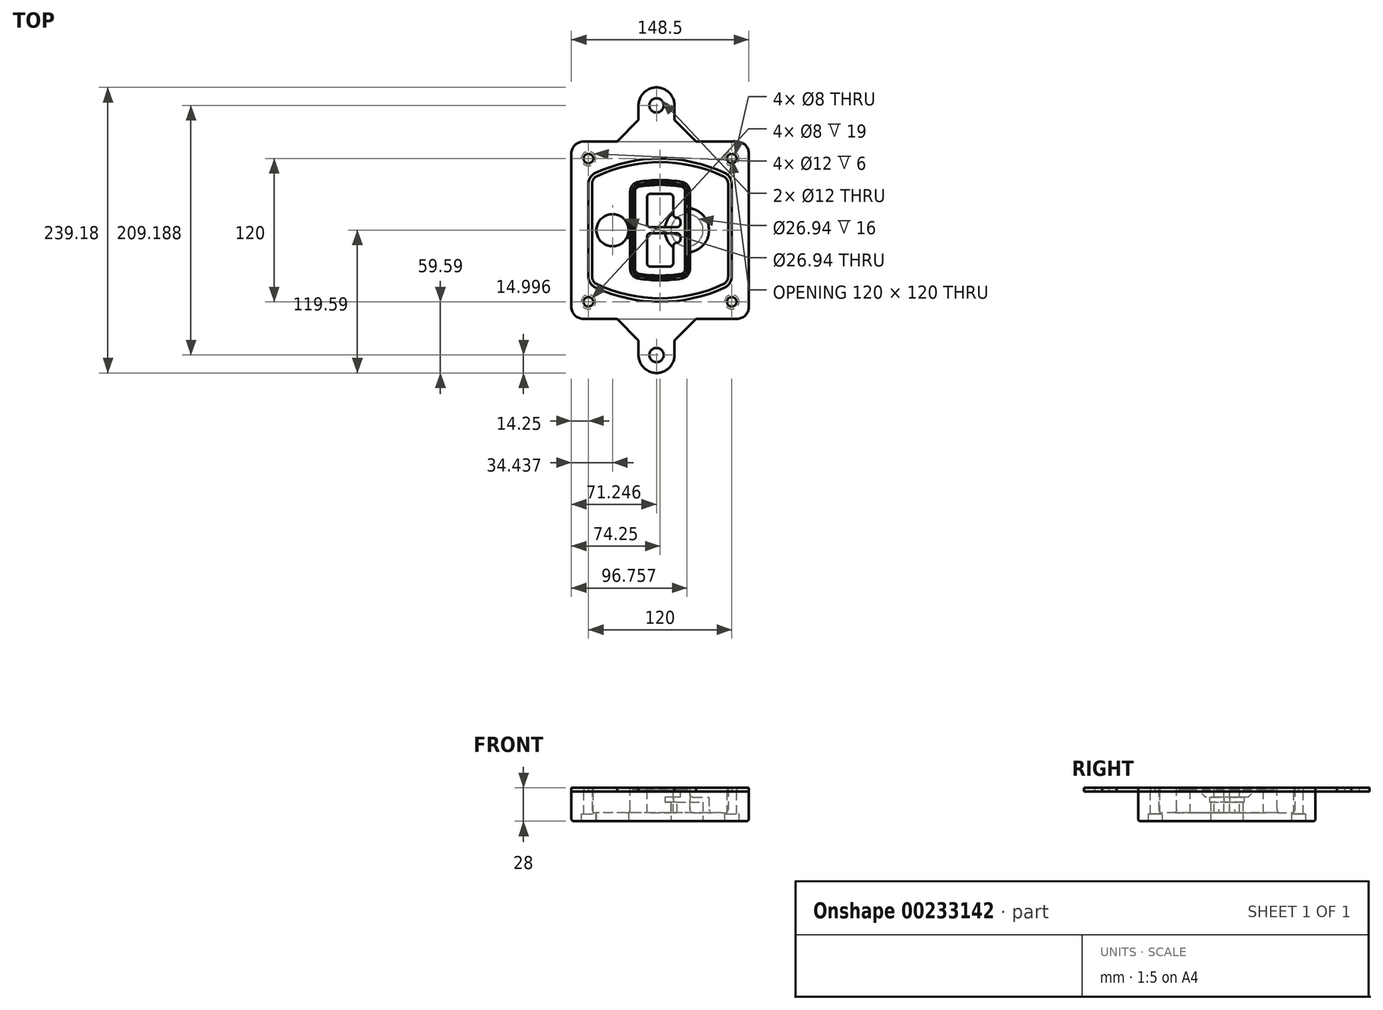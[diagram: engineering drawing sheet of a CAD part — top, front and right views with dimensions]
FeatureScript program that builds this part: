
annotation { "Feature Type Name" : "Feature", "Feature Type Description" : "" }
export const myFeature = defineFeature(function(context is Context, id is Id, definition is map)
    precondition{}
    {
        {
            var Q0;
            Q0=qCreatedBy(makeId("Top.planeOp"),FACE);
            var sketch = newSketch(context, id + "F0", { "sketchPlane" : qUnion([Q0])});
            skPoint(sketch, "E0.rect.middle", {"position": v(0, 0) * mm});
            skLineSegment(sketch, "E1.bottom", {"start": v(-64.25, -74.25) * mm, "end": v(64.25, -74.25) * mm});
            skLineSegment(sketch, "E1.top", {"start": v(-64.25, 74.25) * mm, "end": v(64.25, 74.25) * mm});
            skLineSegment(sketch, "E1.left", {"start": v(-74.25, -64.25) * mm, "end": v(-74.25, 64.25) * mm});
            skLineSegment(sketch, "E1.right", {"start": v(74.25, -64.25) * mm, "end": v(74.25, 64.25) * mm});
            skLineSegment(sketch, "E2", {"start": v(-74.25, 74.25) * mm, "end": v(74.25, -74.25) * mm, "construction": true});
            skLineSegment(sketch, "E3", {"start": v(74.25, 74.25) * mm, "end": v(-74.25, -74.25) * mm, "construction": true});
            skCircle(sketch, "E4", {"center": v(-60, 60) * mm, "radius": 4 * mm});
            skCircle(sketch, "E5", {"center": v(60, 60) * mm, "radius": 4 * mm});
            skCircle(sketch, "E6", {"center": v(60, -60) * mm, "radius": 4 * mm});
            skCircle(sketch, "E7", {"center": v(-60, -60) * mm, "radius": 4 * mm});
            skLineSegment(sketch, "E8", {"start": v(-60, 60) * mm, "end": v(60, 60) * mm, "construction": true});
            skLineSegment(sketch, "E9", {"start": v(60, 60) * mm, "end": v(60, -60) * mm, "construction": true});
            skLineSegment(sketch, "E10", {"start": v(60, -60) * mm, "end": v(-60, -60) * mm, "construction": true});
            skLineSegment(sketch, "E11", {"start": v(-60, -60) * mm, "end": v(-60, 60) * mm, "construction": true});
            skLineSegment(sketch, "E12", {"start": v(-60, 38.83) * mm, "end": v(-60, -38.83) * mm});
            skLineSegment(sketch, "E13", {"start": v(60, 38.83) * mm, "end": v(60, -38.83) * mm});
            skArc(sketch, "E14", {"start": v(54.26, 47.88) * mm, "mid": v(0, 60) * mm, "end": v(-54.26, 47.88) * mm});
            skArc(sketch, "E15", {"start": v(-54.26, -47.88) * mm, "mid": v(0, -60) * mm, "end": v(54.26, -47.88) * mm});
            skLineSegment(sketch, "E16", {"start": v(-60, 0) * mm, "end": v(60, 0) * mm, "construction": true});
            skPoint(sketch, "E17.visualSharp", {"position": v(-60, -45) * mm});
            skArc(sketch, "E17.filletArc", {"start": v(-60, -38.83) * mm, "mid": v(-58.44, -44.2) * mm, "end": v(-54.26, -47.88) * mm});
            skPoint(sketch, "E18.visualSharp", {"position": v(-60, 45) * mm});
            skArc(sketch, "E18.filletArc", {"start": v(-54.26, 47.88) * mm, "mid": v(-58.44, 44.2) * mm, "end": v(-60, 38.83) * mm});
            skPoint(sketch, "E19.visualSharp", {"position": v(60, 45) * mm});
            skArc(sketch, "E19.filletArc", {"start": v(60, 38.83) * mm, "mid": v(58.44, 44.2) * mm, "end": v(54.26, 47.88) * mm});
            skPoint(sketch, "E20.visualSharp", {"position": v(60, -45) * mm});
            skArc(sketch, "E20.filletArc", {"start": v(54.26, -47.88) * mm, "mid": v(58.44, -44.2) * mm, "end": v(60, -38.83) * mm});
            skPoint(sketch, "E21.visualSharp", {"position": v(-74.25, 74.25) * mm});
            skArc(sketch, "E21.filletArc", {"start": v(-64.25, 74.25) * mm, "mid": v(-71.32, 71.32) * mm, "end": v(-74.25, 64.25) * mm});
            skPoint(sketch, "E22.visualSharp", {"position": v(74.25, 74.25) * mm});
            skArc(sketch, "E22.filletArc", {"start": v(74.25, 64.25) * mm, "mid": v(71.32, 71.32) * mm, "end": v(64.25, 74.25) * mm});
            skPoint(sketch, "E23.visualSharp", {"position": v(74.25, -74.25) * mm});
            skArc(sketch, "E23.filletArc", {"start": v(64.25, -74.25) * mm, "mid": v(71.32, -71.32) * mm, "end": v(74.25, -64.25) * mm});
            skPoint(sketch, "E24.visualSharp", {"position": v(-74.25, -74.25) * mm});
            skArc(sketch, "E24.filletArc", {"start": v(-74.25, -64.25) * mm, "mid": v(-71.32, -71.32) * mm, "end": v(-64.25, -74.25) * mm});
            skArc(sketch, "E25.0", {"start": v(57, 38.83) * mm, "mid": v(55.9, 42.58) * mm, "end": v(52.98, 45.17) * mm});
            skLineSegment(sketch, "E25.1", {"start": v(57, 38.83) * mm, "end": v(57, -38.83) * mm});
            skArc(sketch, "E25.2", {"start": v(52.98, -45.17) * mm, "mid": v(55.9, -42.58) * mm, "end": v(57, -38.83) * mm});
            skArc(sketch, "E25.3", {"start": v(-52.98, -45.17) * mm, "mid": v(0, -57) * mm, "end": v(52.98, -45.17) * mm});
            skArc(sketch, "E25.4", {"start": v(-57, -38.83) * mm, "mid": v(-55.9, -42.58) * mm, "end": v(-52.98, -45.17) * mm});
            skArc(sketch, "E25.5", {"start": v(52.98, 45.17) * mm, "mid": v(0, 57) * mm, "end": v(-52.98, 45.17) * mm});
            skLineSegment(sketch, "E25.6", {"start": v(-57, 38.83) * mm, "end": v(-57, -38.83) * mm});
            skArc(sketch, "E25.7", {"start": v(-52.98, 45.17) * mm, "mid": v(-55.9, 42.58) * mm, "end": v(-57, 38.83) * mm});
            skArc(sketch, "E26.0", {"start": v(-55.96, 51.5) * mm, "mid": v(-61.82, 46.33) * mm, "end": v(-64, 38.83) * mm});
            skArc(sketch, "E26.1", {"start": v(55.96, 51.5) * mm, "mid": v(0, 64) * mm, "end": v(-55.96, 51.5) * mm});
            skArc(sketch, "E26.2", {"start": v(64, 38.83) * mm, "mid": v(61.82, 46.33) * mm, "end": v(55.96, 51.5) * mm});
            skLineSegment(sketch, "E26.3", {"start": v(64, 38.83) * mm, "end": v(64, -38.83) * mm});
            skArc(sketch, "E26.4", {"start": v(55.96, -51.5) * mm, "mid": v(61.82, -46.33) * mm, "end": v(64, -38.83) * mm});
            skLineSegment(sketch, "E26.5", {"start": v(-64, 38.83) * mm, "end": v(-64, -38.83) * mm});
            skArc(sketch, "E26.6", {"start": v(-55.96, -51.5) * mm, "mid": v(0, -64) * mm, "end": v(55.96, -51.5) * mm});
            skArc(sketch, "E26.7", {"start": v(-64, -38.83) * mm, "mid": v(-61.82, -46.33) * mm, "end": v(-55.96, -51.5) * mm});
            skSolve(sketch);
        }
        {
            var Q0;
            Q0=makeQuery(id+"F0.imprint","IMPRINT",FACE,{"disambiguationData":[TD([[makeQuery(id+"F0.imprint","IMPRINT",EDGE,{"derivedFrom":sQuery(id+"F0.wireOp",EDGE,"E1.bottom")}),1.0]])]});
            var Q1;
            Q1=makeQuery(id+"F0.imprint","IMPRINT",FACE,{"disambiguationData":[TD([[makeQuery(id+"F0.imprint","IMPRINT",EDGE,{"derivedFrom":sQuery(id+"F0.wireOp",EDGE,"E12")}),1.0]])]});
            var Q2;
            Q2=makeQuery(id+"F0.imprint","IMPRINT",FACE,{"disambiguationData":[TD([[makeQuery(id+"F0.imprint","IMPRINT",EDGE,{"derivedFrom":sQuery(id+"F0.wireOp",EDGE,"E25.0")}),1.0]])]});
            var Q3;
            Q3=makeQuery(id+"F0.imprint","IMPRINT",FACE,{"disambiguationData":[TD([[makeQuery(id+"F0.imprint","IMPRINT",EDGE,{"derivedFrom":sQuery(id+"F0.wireOp",EDGE,"E12")}),-1.0]])]});
            extrude(context, id + "F1", {"entities" : qUnion([Q0, Q1, Q2, Q3]), "oppositeDirection" : true, "depth" : 25 * mm});
        }
        {
            var Q0;
            Q0=makeQuery(id+"F0.imprint","IMPRINT",FACE,{"disambiguationData":[TD([[makeQuery(id+"F0.imprint","IMPRINT",EDGE,{"derivedFrom":sQuery(id+"F0.wireOp",EDGE,"E12")}),1.0]])]});
            extrude(context, id + "F2", {"entities" : qUnion([Q0]), "operationType" : NewBodyOperationType.ADD, "depth" : 3 * mm});
        }
        {
            var Q0;
            Q0=makeQuery(id+"F0.imprint","IMPRINT",FACE,{"disambiguationData":[TD([[makeQuery(id+"F0.imprint","IMPRINT",EDGE,{"derivedFrom":sQuery(id+"F0.wireOp",EDGE,"E25.0")}),1.0]])]});
            extrude(context, id + "F3", {"entities" : qUnion([Q0]), "operationType" : NewBodyOperationType.REMOVE, "oppositeDirection" : true, "depth" : 18 * mm});
        }
        {
            var Q0;
            Q0=makeQuery(id+"F2.opExtrude","CAP_FACE",FACE,{"disambiguationData":[OSD([sQuery(id+"F0.wireOp",EDGE,"E12"),sQuery(id+"F0.wireOp",EDGE,"E13"),sQuery(id+"F0.wireOp",EDGE,"E14"),sQuery(id+"F0.wireOp",EDGE,"E15"),sQuery(id+"F0.wireOp",EDGE,"E17.filletArc"),sQuery(id+"F0.wireOp",EDGE,"E18.filletArc"),sQuery(id+"F0.wireOp",EDGE,"E19.filletArc"),sQuery(id+"F0.wireOp",EDGE,"E20.filletArc"),sQuery(id+"F0.wireOp",EDGE,"E25.0"),sQuery(id+"F0.wireOp",EDGE,"E25.1"),sQuery(id+"F0.wireOp",EDGE,"E25.2"),sQuery(id+"F0.wireOp",EDGE,"E25.3"),sQuery(id+"F0.wireOp",EDGE,"E25.4"),sQuery(id+"F0.wireOp",EDGE,"E25.5"),sQuery(id+"F0.wireOp",EDGE,"E25.6"),sQuery(id+"F0.wireOp",EDGE,"E25.7")])],"isStart":false});
            var sketch = newSketch(context, id + "F4", { "sketchPlane" : qUnion([Q0])});
            skArc(sketch, "E27.0", {"start": v(-18.34, -40.45) * mm, "mid": v(0, -42) * mm, "end": v(18.34, -40.45) * mm});
            skArc(sketch, "E28.0", {"start": v(18.34, 40.45) * mm, "mid": v(0, 42) * mm, "end": v(-18.34, 40.45) * mm});
            skLineSegment(sketch, "E29", {"start": v(-25, 32.57) * mm, "end": v(-25, -32.57) * mm});
            skLineSegment(sketch, "E30", {"start": v(25, 32.57) * mm, "end": v(25, -32.57) * mm});
            skLineSegment(sketch, "E31", {"start": v(-25, 39.1) * mm, "end": v(25, 39.1) * mm, "construction": true});
            skLineSegment(sketch, "E32", {"start": v(-25, -39.1) * mm, "end": v(25, -39.1) * mm, "construction": true});
            skPoint(sketch, "E33.visualSharp", {"position": v(-25, 39.1) * mm});
            skArc(sketch, "E33.filletArc", {"start": v(-18.34, 40.45) * mm, "mid": v(-23.11, 37.73) * mm, "end": v(-25, 32.57) * mm});
            skPoint(sketch, "E34.visualSharp", {"position": v(25, 39.1) * mm});
            skArc(sketch, "E34.filletArc", {"start": v(25, 32.57) * mm, "mid": v(23.11, 37.73) * mm, "end": v(18.34, 40.45) * mm});
            skPoint(sketch, "E35.visualSharp", {"position": v(25, -39.1) * mm});
            skArc(sketch, "E35.filletArc", {"start": v(18.34, -40.45) * mm, "mid": v(23.11, -37.73) * mm, "end": v(25, -32.57) * mm});
            skPoint(sketch, "E36.visualSharp", {"position": v(-25, -39.1) * mm});
            skArc(sketch, "E36.filletArc", {"start": v(-25, -32.57) * mm, "mid": v(-23.11, -37.73) * mm, "end": v(-18.34, -40.45) * mm});
            skArc(sketch, "E37.0", {"start": v(52.98, 45.17) * mm, "mid": v(0, 57) * mm, "end": v(-52.98, 45.17) * mm});
            skArc(sketch, "E37.1", {"start": v(-52.98, 45.17) * mm, "mid": v(-55.9, 42.58) * mm, "end": v(-57, 38.83) * mm});
            skLineSegment(sketch, "E37.2", {"start": v(-57, 38.83) * mm, "end": v(-57, -38.83) * mm});
            skArc(sketch, "E37.3", {"start": v(-57, -38.83) * mm, "mid": v(-55.9, -42.58) * mm, "end": v(-52.98, -45.17) * mm});
            skArc(sketch, "E37.4", {"start": v(-52.98, -45.17) * mm, "mid": v(0, -57) * mm, "end": v(52.98, -45.17) * mm});
            skArc(sketch, "E37.5", {"start": v(52.98, -45.17) * mm, "mid": v(55.9, -42.58) * mm, "end": v(57, -38.83) * mm});
            skLineSegment(sketch, "E37.6", {"start": v(57, 38.83) * mm, "end": v(57, -38.83) * mm});
            skArc(sketch, "E37.7", {"start": v(57, 38.83) * mm, "mid": v(55.9, 42.58) * mm, "end": v(52.98, 45.17) * mm});
            skLineSegment(sketch, "E38.0", {"start": v(23, 32.57) * mm, "end": v(23, -32.57) * mm});
            skArc(sketch, "E38.1", {"start": v(18, -38.48) * mm, "mid": v(21.58, -36.44) * mm, "end": v(23, -32.57) * mm});
            skArc(sketch, "E38.2", {"start": v(-18, -38.48) * mm, "mid": v(0, -40) * mm, "end": v(18, -38.48) * mm});
            skArc(sketch, "E38.3", {"start": v(-23, -32.57) * mm, "mid": v(-21.58, -36.44) * mm, "end": v(-18, -38.48) * mm});
            skLineSegment(sketch, "E38.4", {"start": v(-23, 32.57) * mm, "end": v(-23, -32.57) * mm});
            skArc(sketch, "E38.5", {"start": v(23, 32.57) * mm, "mid": v(21.58, 36.44) * mm, "end": v(18, 38.48) * mm});
            skArc(sketch, "E38.6", {"start": v(-18, 38.48) * mm, "mid": v(-21.58, 36.44) * mm, "end": v(-23, 32.57) * mm});
            skArc(sketch, "E38.7", {"start": v(18, 38.48) * mm, "mid": v(0, 40) * mm, "end": v(-18, 38.48) * mm});
            skArc(sketch, "E39.0", {"start": v(21, 32.57) * mm, "mid": v(20.06, 35.15) * mm, "end": v(17.67, 36.5) * mm});
            skLineSegment(sketch, "E39.1", {"start": v(21, 32.57) * mm, "end": v(21, -32.57) * mm});
            skArc(sketch, "E39.2", {"start": v(17.67, -36.5) * mm, "mid": v(20.06, -35.15) * mm, "end": v(21, -32.57) * mm});
            skArc(sketch, "E39.3", {"start": v(-17.67, -36.5) * mm, "mid": v(0, -38) * mm, "end": v(17.67, -36.5) * mm});
            skArc(sketch, "E39.4", {"start": v(-21, -32.57) * mm, "mid": v(-20.06, -35.15) * mm, "end": v(-17.67, -36.5) * mm});
            skArc(sketch, "E39.5", {"start": v(17.67, 36.5) * mm, "mid": v(0, 38) * mm, "end": v(-17.67, 36.5) * mm});
            skLineSegment(sketch, "E39.6", {"start": v(-21, 32.57) * mm, "end": v(-21, -32.57) * mm});
            skArc(sketch, "E39.7", {"start": v(-17.67, 36.5) * mm, "mid": v(-20.06, 35.15) * mm, "end": v(-21, 32.57) * mm});
            skLineSegment(sketch, "E40", {"start": v(-25, 0) * mm, "end": v(25, 0) * mm, "construction": true});
            skLineSegment(sketch, "E41", {"start": v(-11, 5.5) * mm, "end": v(-11, 27.5) * mm});
            skLineSegment(sketch, "E42", {"start": v(-8, 30.5) * mm, "end": v(8, 30.5) * mm});
            skLineSegment(sketch, "E43", {"start": v(11, 27.5) * mm, "end": v(11, 13.5) * mm});
            skLineSegment(sketch, "E44", {"start": v(14, 10.5) * mm, "end": v(14, 10.5) * mm});
            skLineSegment(sketch, "E45", {"start": v(17, 7.5) * mm, "end": v(17, 5.5) * mm});
            skLineSegment(sketch, "E46", {"start": v(14, 2.5) * mm, "end": v(-8, 2.5) * mm});
            skPoint(sketch, "E47.visualSharp", {"position": v(-11, 30.5) * mm});
            skArc(sketch, "E47.filletArc", {"start": v(-8, 30.5) * mm, "mid": v(-10.12, 29.62) * mm, "end": v(-11, 27.5) * mm});
            skPoint(sketch, "E48.visualSharp", {"position": v(11, 30.5) * mm});
            skArc(sketch, "E48.filletArc", {"start": v(11, 27.5) * mm, "mid": v(10.12, 29.62) * mm, "end": v(8, 30.5) * mm});
            skPoint(sketch, "E49.visualSharp", {"position": v(11, 10.5) * mm});
            skArc(sketch, "E49.filletArc", {"start": v(11, 13.5) * mm, "mid": v(11.88, 11.38) * mm, "end": v(14, 10.5) * mm});
            skPoint(sketch, "E50.visualSharp", {"position": v(17, 10.5) * mm});
            skArc(sketch, "E50.filletArc", {"start": v(17, 7.5) * mm, "mid": v(16.12, 9.62) * mm, "end": v(14, 10.5) * mm});
            skPoint(sketch, "E51.visualSharp", {"position": v(17, 2.5) * mm});
            skArc(sketch, "E51.filletArc", {"start": v(14, 2.5) * mm, "mid": v(16.12, 3.38) * mm, "end": v(17, 5.5) * mm});
            skPoint(sketch, "E52.visualSharp", {"position": v(-11, 2.5) * mm});
            skArc(sketch, "E52.filletArc", {"start": v(-11, 5.5) * mm, "mid": v(-10.12, 3.38) * mm, "end": v(-8, 2.5) * mm});
            skLineSegment(sketch, "E53.0.MirrorCS", {"start": v(14, -2.5) * mm, "end": v(-8, -2.5) * mm});
            skArc(sketch, "E54.0.MirrorCS", {"start": v(-11, -5.5) * mm, "mid": v(-10.12, -3.38) * mm, "end": v(-8, -2.5) * mm});
            skLineSegment(sketch, "E55.0.MirrorCS", {"start": v(-11, -5.5) * mm, "end": v(-11, -27.5) * mm});
            skArc(sketch, "E56.0.MirrorCS", {"start": v(-8, -30.5) * mm, "mid": v(-10.12, -29.62) * mm, "end": v(-11, -27.5) * mm});
            skLineSegment(sketch, "E57.0.MirrorCS", {"start": v(-8, -30.5) * mm, "end": v(8, -30.5) * mm});
            skArc(sketch, "E58.0.MirrorCS", {"start": v(11, -27.5) * mm, "mid": v(10.12, -29.62) * mm, "end": v(8, -30.5) * mm});
            skLineSegment(sketch, "E59.0.MirrorCS", {"start": v(11, -27.5) * mm, "end": v(11, -13.5) * mm});
            skArc(sketch, "E60.0.MirrorCS", {"start": v(11, -13.5) * mm, "mid": v(11.88, -11.38) * mm, "end": v(14, -10.5) * mm});
            skArc(sketch, "E61.0.MirrorCS", {"start": v(17, -7.5) * mm, "mid": v(16.12, -9.62) * mm, "end": v(14, -10.5) * mm});
            skLineSegment(sketch, "E62.0.MirrorCS", {"start": v(17, -7.5) * mm, "end": v(17, -5.5) * mm});
            skArc(sketch, "E63.0.MirrorCS", {"start": v(14, -2.5) * mm, "mid": v(16.12, -3.38) * mm, "end": v(17, -5.5) * mm});
            skSolve(sketch);
        }
        {
            var Q0;
            Q0=makeQuery(id+"F4.imprint","IMPRINT",FACE,{"disambiguationData":[TD([[makeQuery(id+"F4.imprint","IMPRINT",EDGE,{"derivedFrom":sQuery(id+"F4.wireOp",EDGE,"E27.0")}),1.0]])]});
            var Q1;
            Q1=makeQuery(id+"F4.imprint","IMPRINT",FACE,{"disambiguationData":[TD([[makeQuery(id+"F4.imprint","IMPRINT",EDGE,{"derivedFrom":sQuery(id+"F4.wireOp",EDGE,"E38.0")}),-1.0]])]});
            var Q2;
            Q2=makeQuery(id+"F4.imprint","IMPRINT",FACE,{"disambiguationData":[TD([[makeQuery(id+"F4.imprint","IMPRINT",EDGE,{"derivedFrom":sQuery(id+"F4.wireOp",EDGE,"E39.0")}),1.0]])]});
            extrude(context, id + "F5", {"entities" : qUnion([Q0, Q1, Q2]), "operationType" : NewBodyOperationType.ADD, "endBound" : BoundingType.UP_TO_NEXT, "oppositeDirection" : true, "depth" : 25 * mm});
        }
        {
            var Q0;
            Q0=makeQuery(id+"F4.imprint","IMPRINT",FACE,{"disambiguationData":[TD([[makeQuery(id+"F4.imprint","IMPRINT",EDGE,{"derivedFrom":sQuery(id+"F4.wireOp",EDGE,"E38.0")}),-1.0]])]});
            extrude(context, id + "F6", {"entities" : qUnion([Q0]), "operationType" : NewBodyOperationType.REMOVE, "oppositeDirection" : true, "depth" : 2 * mm});
        }
        {
            var Q0;
            Q0=makeQuery(id+"F1.opExtrude","CAP_FACE",FACE,{"disambiguationData":[OSD([sQuery(id+"F0.wireOp",EDGE,"E1.bottom"),sQuery(id+"F0.wireOp",EDGE,"E1.top"),sQuery(id+"F0.wireOp",EDGE,"E1.left"),sQuery(id+"F0.wireOp",EDGE,"E1.right"),sQuery(id+"F0.wireOp",EDGE,"E4"),sQuery(id+"F0.wireOp",EDGE,"E5"),sQuery(id+"F0.wireOp",EDGE,"E6"),sQuery(id+"F0.wireOp",EDGE,"E7"),sQuery(id+"F0.wireOp",EDGE,"E21.filletArc"),sQuery(id+"F0.wireOp",EDGE,"E22.filletArc"),sQuery(id+"F0.wireOp",EDGE,"E23.filletArc"),sQuery(id+"F0.wireOp",EDGE,"E24.filletArc")])],"isStart":false});
            var sketch = newSketch(context, id + "F7", { "sketchPlane" : qUnion([Q0])});
            skCircle(sketch, "E64", {"center": v(22.5, 0) * mm, "radius": 13.47 * mm});
            skCircle(sketch, "E65", {"center": v(-39.81, 0) * mm, "radius": 13.47 * mm});
            skLineSegment(sketch, "E66", {"start": v(74.25, 0) * mm, "end": v(-74.25, 0) * mm});
            skCircle(sketch, "E67", {"center": v(22.5, 0) * mm, "radius": 18.47 * mm});
            skCircle(sketch, "E68", {"center": v(60, -60) * mm, "radius": 6 * mm});
            skCircle(sketch, "E69", {"center": v(-60, -60) * mm, "radius": 6 * mm});
            skCircle(sketch, "E70", {"center": v(-60, 60) * mm, "radius": 6 * mm});
            skCircle(sketch, "E71", {"center": v(60, 60) * mm, "radius": 6 * mm});
            skSolve(sketch);
        }
        {
            var Q0;
            {var subQ1=sQuery(id+"F7.wireOp",EDGE,"E66");var subQ4=sQuery(id+"F7.wireOp",EDGE,"E64");var subQ6=makeQuery(id+"F7.imprint","INTERSECT",VERTEX,{"disambiguationData":[OD(0.0)],"derivedFrom":[subQ4,subQ1]});Q0=makeQuery(id+"F7.imprint","IMPRINT",FACE,{"disambiguationData":[TD([[makeQuery(id+"F7.imprint","IMPRINT",EDGE,{"disambiguationData":[TD([[subQ6,-1.0]])],"derivedFrom":subQ4}),-1.0]])]});}
            var Q1;
            {var subQ0=sQuery(id+"F7.wireOp",EDGE,"E66");var subQ1=sQuery(id+"F7.wireOp",EDGE,"E64");var subQ3=makeQuery(id+"F7.imprint","INTERSECT",VERTEX,{"disambiguationData":[OD(0.0)],"derivedFrom":[subQ1,subQ0]});Q1=makeQuery(id+"F7.imprint","IMPRINT",FACE,{"disambiguationData":[TD([[makeQuery(id+"F7.imprint","IMPRINT",EDGE,{"disambiguationData":[TD([[subQ3,-1.0]])],"derivedFrom":subQ1}),1.0]])]});}
            var Q2;
            {var subQ0=sQuery(id+"F7.wireOp",EDGE,"E66");var subQ1=sQuery(id+"F7.wireOp",EDGE,"E64");var subQ3=makeQuery(id+"F7.imprint","INTERSECT",VERTEX,{"disambiguationData":[OD(0.0)],"derivedFrom":[subQ1,subQ0]});Q2=makeQuery(id+"F7.imprint","IMPRINT",FACE,{"disambiguationData":[TD([[makeQuery(id+"F7.imprint","IMPRINT",EDGE,{"disambiguationData":[TD([[subQ3,1.0]])],"derivedFrom":subQ1}),1.0]])]});}
            var Q3;
            {var subQ1=sQuery(id+"F7.wireOp",EDGE,"E66");var subQ4=sQuery(id+"F7.wireOp",EDGE,"E64");var subQ6=makeQuery(id+"F7.imprint","INTERSECT",VERTEX,{"disambiguationData":[OD(0.0)],"derivedFrom":[subQ4,subQ1]});Q3=makeQuery(id+"F7.imprint","IMPRINT",FACE,{"disambiguationData":[TD([[makeQuery(id+"F7.imprint","IMPRINT",EDGE,{"disambiguationData":[TD([[subQ6,1.0]])],"derivedFrom":subQ4}),-1.0]])]});}
            extrude(context, id + "F8", {"entities" : qUnion([Q0, Q1, Q2, Q3]), "operationType" : NewBodyOperationType.ADD, "oppositeDirection" : true, "depth" : 20 * mm});
        }
        {
            var Q0;
            {var subQ0=sQuery(id+"F7.wireOp",EDGE,"E66");var subQ1=sQuery(id+"F7.wireOp",EDGE,"E64");var subQ3=makeQuery(id+"F7.imprint","INTERSECT",VERTEX,{"disambiguationData":[OD(0.0)],"derivedFrom":[subQ1,subQ0]});Q0=makeQuery(id+"F7.imprint","IMPRINT",FACE,{"disambiguationData":[TD([[makeQuery(id+"F7.imprint","IMPRINT",EDGE,{"disambiguationData":[TD([[subQ3,-1.0]])],"derivedFrom":subQ1}),1.0]])]});}
            var Q1;
            {var subQ0=sQuery(id+"F7.wireOp",EDGE,"E66");var subQ1=sQuery(id+"F7.wireOp",EDGE,"E64");var subQ3=makeQuery(id+"F7.imprint","INTERSECT",VERTEX,{"disambiguationData":[OD(0.0)],"derivedFrom":[subQ1,subQ0]});Q1=makeQuery(id+"F7.imprint","IMPRINT",FACE,{"disambiguationData":[TD([[makeQuery(id+"F7.imprint","IMPRINT",EDGE,{"disambiguationData":[TD([[subQ3,1.0]])],"derivedFrom":subQ1}),1.0]])]});}
            extrude(context, id + "F9", {"entities" : qUnion([Q0, Q1]), "operationType" : NewBodyOperationType.REMOVE, "oppositeDirection" : true, "depth" : 16 * mm});
        }
        {
            var Q0;
            {var subQ0=sQuery(id+"F7.wireOp",EDGE,"E66");var subQ1=sQuery(id+"F7.wireOp",EDGE,"E65");var subQ3=makeQuery(id+"F7.imprint","INTERSECT",VERTEX,{"disambiguationData":[OD(0.0)],"derivedFrom":[subQ1,subQ0]});Q0=makeQuery(id+"F7.imprint","IMPRINT",FACE,{"disambiguationData":[TD([[makeQuery(id+"F7.imprint","IMPRINT",EDGE,{"disambiguationData":[TD([[subQ3,-1.0]])],"derivedFrom":subQ1}),1.0]])]});}
            var Q1;
            {var subQ0=sQuery(id+"F7.wireOp",EDGE,"E66");var subQ1=sQuery(id+"F7.wireOp",EDGE,"E65");var subQ3=makeQuery(id+"F7.imprint","INTERSECT",VERTEX,{"disambiguationData":[OD(0.0)],"derivedFrom":[subQ1,subQ0]});Q1=makeQuery(id+"F7.imprint","IMPRINT",FACE,{"disambiguationData":[TD([[makeQuery(id+"F7.imprint","IMPRINT",EDGE,{"disambiguationData":[TD([[subQ3,1.0]])],"derivedFrom":subQ1}),1.0]])]});}
            extrude(context, id + "F10", {"entities" : qUnion([Q0, Q1]), "operationType" : NewBodyOperationType.REMOVE, "oppositeDirection" : true, "depth" : 25 * mm});
        }
        {
            var Q0;
            Q0=makeQuery(id+"F7.imprint","IMPRINT",FACE,{"disambiguationData":[TD([[makeQuery(id+"F7.imprint","IMPRINT",EDGE,{"derivedFrom":sQuery(id+"F7.wireOp",EDGE,"E68")}),1.0]])]});
            var Q1;
            Q1=makeQuery(id+"F7.imprint","IMPRINT",FACE,{"disambiguationData":[TD([[makeQuery(id+"F7.imprint","IMPRINT",EDGE,{"derivedFrom":makeQuery(id+"F1.opExtrude","CAP_EDGE",EDGE,{"disambiguationData":[OSD([sQuery(id+"F0.wireOp",EDGE,"E5")])],"isStart":false})}),-1.0]])]});
            var Q2;
            Q2=makeQuery(id+"F7.imprint","IMPRINT",FACE,{"disambiguationData":[TD([[makeQuery(id+"F7.imprint","IMPRINT",EDGE,{"derivedFrom":sQuery(id+"F7.wireOp",EDGE,"E69")}),1.0]])]});
            var Q3;
            Q3=makeQuery(id+"F7.imprint","IMPRINT",FACE,{"disambiguationData":[TD([[makeQuery(id+"F7.imprint","IMPRINT",EDGE,{"derivedFrom":makeQuery(id+"F1.opExtrude","CAP_EDGE",EDGE,{"disambiguationData":[OSD([sQuery(id+"F0.wireOp",EDGE,"E4")])],"isStart":false})}),-1.0]])]});
            var Q4;
            Q4=makeQuery(id+"F7.imprint","IMPRINT",FACE,{"disambiguationData":[TD([[makeQuery(id+"F7.imprint","IMPRINT",EDGE,{"derivedFrom":sQuery(id+"F7.wireOp",EDGE,"E70")}),1.0]])]});
            var Q5;
            Q5=makeQuery(id+"F7.imprint","IMPRINT",FACE,{"disambiguationData":[TD([[makeQuery(id+"F7.imprint","IMPRINT",EDGE,{"derivedFrom":makeQuery(id+"F1.opExtrude","CAP_EDGE",EDGE,{"disambiguationData":[OSD([sQuery(id+"F0.wireOp",EDGE,"E7")])],"isStart":false})}),-1.0]])]});
            var Q6;
            Q6=makeQuery(id+"F7.imprint","IMPRINT",FACE,{"disambiguationData":[TD([[makeQuery(id+"F7.imprint","IMPRINT",EDGE,{"derivedFrom":sQuery(id+"F7.wireOp",EDGE,"E71")}),1.0]])]});
            var Q7;
            Q7=makeQuery(id+"F7.imprint","IMPRINT",FACE,{"disambiguationData":[TD([[makeQuery(id+"F7.imprint","IMPRINT",EDGE,{"derivedFrom":makeQuery(id+"F1.opExtrude","CAP_EDGE",EDGE,{"disambiguationData":[OSD([sQuery(id+"F0.wireOp",EDGE,"E6")])],"isStart":false})}),-1.0]])]});
            extrude(context, id + "F11", {"entities" : qUnion([Q0, Q1, Q2, Q3, Q4, Q5, Q6, Q7]), "operationType" : NewBodyOperationType.REMOVE, "oppositeDirection" : true, "depth" : 6 * mm});
        }
        {
            var Q0;
            Q0=makeQuery(id+"F9.boolean.opBoolean","COPY",FACE,{"derivedFrom":makeQuery(id+"F9.opExtrude","CAP_FACE",FACE,{"disambiguationData":[OSD([sQuery(id+"F7.wireOp",EDGE,"E64")])],"isStart":false})});
            var sketch = newSketch(context, id + "F12", { "sketchPlane" : qUnion([Q0])});
            skArc(sketch, "E72.0", {"start": v(11, 14.45) * mm, "mid": v(6.45, 9.13) * mm, "end": v(4.2, 2.5) * mm});
            skArc(sketch, "E72.1", {"start": v(4.2, -2.5) * mm, "mid": v(6.45, -9.13) * mm, "end": v(11, -14.45) * mm});
            skLineSegment(sketch, "E73", {"start": v(4.2, -2.5) * mm, "end": v(14, -2.5) * mm});
            skLineSegment(sketch, "E74.0", {"start": v(14, 2.5) * mm, "end": v(4.2, 2.5) * mm});
            skArc(sketch, "E74.1", {"start": v(14, 2.5) * mm, "mid": v(16.12, 3.38) * mm, "end": v(17, 5.5) * mm});
            skLineSegment(sketch, "E74.2", {"start": v(17, 7.5) * mm, "end": v(17, 5.5) * mm});
            skArc(sketch, "E74.3", {"start": v(17, 7.5) * mm, "mid": v(16.12, 9.62) * mm, "end": v(14, 10.5) * mm});
            skArc(sketch, "E74.4", {"start": v(11, 13.5) * mm, "mid": v(11.88, 11.38) * mm, "end": v(14, 10.5) * mm});
            skLineSegment(sketch, "E74.5", {"start": v(11, 14.45) * mm, "end": v(11, 13.5) * mm});
            skLineSegment(sketch, "E74.7", {"start": v(14, -2.5) * mm, "end": v(4.2, -2.5) * mm});
            skArc(sketch, "E74.8", {"start": v(14, -2.5) * mm, "mid": v(16.12, -3.38) * mm, "end": v(17, -5.5) * mm});
            skLineSegment(sketch, "E74.9", {"start": v(17, -7.5) * mm, "end": v(17, -5.5) * mm});
            skArc(sketch, "E74.10", {"start": v(17, -7.5) * mm, "mid": v(16.12, -9.62) * mm, "end": v(14, -10.5) * mm});
            skArc(sketch, "E74.11", {"start": v(11, -13.5) * mm, "mid": v(11.88, -11.38) * mm, "end": v(14, -10.5) * mm});
            skLineSegment(sketch, "E74.12", {"start": v(11, -14.45) * mm, "end": v(11, -13.5) * mm});
            skPoint(sketch, "E75.orphan", {"position": v(11, -27.5) * mm});
            skPoint(sketch, "E76.orphan", {"position": v(-8, -2.5) * mm});
            skPoint(sketch, "E77.orphan", {"position": v(-8, 2.5) * mm});
            skPoint(sketch, "E78.orphan", {"position": v(11, 27.5) * mm});
            skSolve(sketch);
        }
        {
            var Q0;
            {var subQ7=sQuery(id+"F12.wireOp",EDGE,"E72.0");var subQ14=sQuery(id+"F12.wireOp",EDGE,"E72.1");var subQ16=sQuery(id+"F12.wireOp",EDGE,"E74.1");var subQ18=sQuery(id+"F12.wireOp",EDGE,"E74.8");Q0=qUnion([makeQuery(id+"F12.imprint","IMPRINT",FACE,{"disambiguationData":[TD([[makeQuery(id+"F12.imprint","IMPRINT",EDGE,{"derivedFrom":subQ7}),1.0]])]}),makeQuery(id+"F12.imprint","IMPRINT",FACE,{"disambiguationData":[TD([[makeQuery(id+"F12.imprint","IMPRINT",EDGE,{"derivedFrom":subQ14}),1.0]])]}),makeQuery(id+"F12.imprint","IMPRINT",FACE,{"disambiguationData":[TD([[makeQuery(id+"F12.imprint","IMPRINT",EDGE,{"derivedFrom":subQ16}),1.0]])]}),makeQuery(id+"F12.imprint","IMPRINT",FACE,{"disambiguationData":[TD([[makeQuery(id+"F12.imprint","IMPRINT",EDGE,{"derivedFrom":subQ18}),-1.0]])]})]);}
            var Q1;
            Q1=makeQuery(id+"F5.boolean.opBoolean","SPLIT",FACE,{"disambiguationData":[TD([makeQuery(id+"F5.opExtrude","SWEPT_FACE",FACE,{"disambiguationData":[OSD([sQuery(id+"F4.wireOp",EDGE,"E41")])]})])],"derivedFrom":makeQuery(id+"F3.boolean.opBoolean","COPY",FACE,{"derivedFrom":makeQuery(id+"F3.opExtrude","CAP_FACE",FACE,{"disambiguationData":[OSD([sQuery(id+"F0.wireOp",EDGE,"E25.0"),sQuery(id+"F0.wireOp",EDGE,"E25.1"),sQuery(id+"F0.wireOp",EDGE,"E25.2"),sQuery(id+"F0.wireOp",EDGE,"E25.3"),sQuery(id+"F0.wireOp",EDGE,"E25.4"),sQuery(id+"F0.wireOp",EDGE,"E25.5"),sQuery(id+"F0.wireOp",EDGE,"E25.6"),sQuery(id+"F0.wireOp",EDGE,"E25.7")])],"isStart":false})})});
            extrude(context, id + "F13", {"entities" : qUnion([Q0]), "operationType" : NewBodyOperationType.REMOVE, "endBound" : BoundingType.UP_TO_SURFACE, "endBoundEntityFace" : qUnion([Q1]), "depth" : 25 * mm});
        }
        {
            var Q0;
            Q0=makeQuery(id+"F3.boolean.opBoolean","COPY",EDGE,{"derivedFrom":makeQuery(id+"F3.opExtrude","CAP_EDGE",EDGE,{"disambiguationData":[OSD([sQuery(id+"F0.wireOp",EDGE,"E25.6")])],"isStart":false})});
            var Q1;
            Q1=makeQuery(id+"F8.boolean.opBoolean","INTERSECT",EDGE,{"derivedFrom":[makeQuery(id+"F5.opExtrude","SWEPT_FACE",FACE,{"disambiguationData":[OSD([sQuery(id+"F4.wireOp",EDGE,"E30")])]}),makeQuery(id+"F8.opExtrude","CAP_FACE",FACE,{"disambiguationData":[OSD([sQuery(id+"F7.wireOp",EDGE,"E67")])],"isStart":false})]});
            var Q2;
            Q2=makeQuery(id+"F8.boolean.opBoolean","INTERSECT",EDGE,{"disambiguationData":[OD(1.0)],"derivedFrom":[makeQuery(id+"F5.opExtrude","SWEPT_FACE",FACE,{"disambiguationData":[OSD([sQuery(id+"F4.wireOp",EDGE,"E30")])]}),makeQuery(id+"F8.opExtrude","SWEPT_FACE",FACE,{"disambiguationData":[OSD([sQuery(id+"F7.wireOp",EDGE,"E67")])]})]});
            var Q3;
            {var subQ0=sQuery(id+"F4.wireOp",EDGE,"E30");Q3=makeQuery(id+"F8.boolean.opBoolean","SPLIT",EDGE,{"disambiguationData":[TD([makeQuery(id+"F5.opExtrude","SWEPT_FACE",FACE,{"disambiguationData":[OSD([sQuery(id+"F4.wireOp",EDGE,"E35.filletArc")])]})])],"derivedFrom":makeQuery(id+"F5.opExtrude","CAP_EDGE",EDGE,{"disambiguationData":[OSD([subQ0])],"isStart":false})});}
            var Q4;
            {var subQ0=sQuery(id+"F0.wireOp",EDGE,"E25.7");var subQ1=sQuery(id+"F0.wireOp",EDGE,"E25.1");var subQ2=sQuery(id+"F0.wireOp",EDGE,"E25.6");var subQ3=sQuery(id+"F0.wireOp",EDGE,"E25.5");var subQ4=sQuery(id+"F0.wireOp",EDGE,"E25.4");var subQ5=sQuery(id+"F0.wireOp",EDGE,"E25.0");var subQ6=sQuery(id+"F0.wireOp",EDGE,"E25.2");var subQ7=sQuery(id+"F0.wireOp",EDGE,"E25.3");Q4=makeQuery(id+"F8.boolean.opBoolean","INTERSECT",EDGE,{"derivedFrom":[makeQuery(id+"F5.boolean.opBoolean","SPLIT",FACE,{"disambiguationData":[TD([makeQuery(id+"F2.opExtrude","SWEPT_FACE",FACE,{"disambiguationData":[OSD([subQ5])]})])],"derivedFrom":makeQuery(id+"F3.boolean.opBoolean","COPY",FACE,{"derivedFrom":makeQuery(id+"F3.opExtrude","CAP_FACE",FACE,{"disambiguationData":[OSD([subQ5,subQ1,subQ6,subQ7,subQ4,subQ3,subQ2,subQ0])],"isStart":false})})}),makeQuery(id+"F8.opExtrude","SWEPT_FACE",FACE,{"disambiguationData":[OSD([sQuery(id+"F7.wireOp",EDGE,"E67")])]})]});}
            var Q5;
            Q5=makeQuery(id+"F8.boolean.opBoolean","INTERSECT",EDGE,{"disambiguationData":[OD(0.0)],"derivedFrom":[makeQuery(id+"F5.opExtrude","SWEPT_FACE",FACE,{"disambiguationData":[OSD([sQuery(id+"F4.wireOp",EDGE,"E30")])]}),makeQuery(id+"F8.opExtrude","SWEPT_FACE",FACE,{"disambiguationData":[OSD([sQuery(id+"F7.wireOp",EDGE,"E67")])]})]});
            fillet(context, id + "F14", {"entities" : qUnion([Q0, Q1, Q2, Q3, Q4, Q5]), "radius" : 3 * mm, "tangentPropagation" : true, "allowEdgeOverflow" : false});
        }
        {
            var Q0;
            Q0=makeQuery(id+"F1.opExtrude","CAP_EDGE",EDGE,{"disambiguationData":[OSD([sQuery(id+"F0.wireOp",EDGE,"E1.bottom")])],"isStart":false});
            fillet(context, id + "F15", {"entities" : qUnion([Q0]), "radius" : 2 * mm, "tangentPropagation" : true, "allowEdgeOverflow" : false});
        }
        {
            var Q0;
            {var subQ0=sQuery(id+"F0.wireOp",EDGE,"E22.filletArc");var subQ1=sQuery(id+"F0.wireOp",EDGE,"E7");var subQ2=sQuery(id+"F0.wireOp",EDGE,"E6");var subQ3=sQuery(id+"F0.wireOp",EDGE,"E5");var subQ4=sQuery(id+"F0.wireOp",EDGE,"E4");var subQ5=sQuery(id+"F0.wireOp",EDGE,"E1.bottom");var subQ6=sQuery(id+"F0.wireOp",EDGE,"E21.filletArc");var subQ7=sQuery(id+"F0.wireOp",EDGE,"E1.top");var subQ8=sQuery(id+"F0.wireOp",EDGE,"E1.left");var subQ9=sQuery(id+"F0.wireOp",EDGE,"E1.right");var subQ10=sQuery(id+"F0.wireOp",EDGE,"E23.filletArc");var subQ11=sQuery(id+"F0.wireOp",EDGE,"E24.filletArc");Q0=makeQuery(id+"F2.boolean.opBoolean","SPLIT",FACE,{"disambiguationData":[TD([makeQuery(id+"F1.opExtrude","SWEPT_FACE",FACE,{"disambiguationData":[OSD([subQ5])]})])],"derivedFrom":makeQuery(id+"F1.opExtrude","CAP_FACE",FACE,{"disambiguationData":[OSD([subQ5,subQ7,subQ8,subQ9,subQ4,subQ3,subQ2,subQ1,subQ6,subQ0,subQ10,subQ11])],"isStart":true})});}
            var sketch = newSketch(context, id + "F16", { "sketchPlane" : qUnion([Q0])});
            skArc(sketch, "E79", {"start": v(12, 104.25) * mm, "mid": v(-3, 119.6) * mm, "end": v(-18, 104.25) * mm});
            skLineSegment(sketch, "E80", {"start": v(-36, 74.25) * mm, "end": v(-18, 92.25) * mm});
            skLineSegment(sketch, "E81", {"start": v(-18, 104.25) * mm, "end": v(-18, 92.25) * mm});
            skLineSegment(sketch, "E82", {"start": v(12, 104.25) * mm, "end": v(12, 92.25) * mm});
            skLineSegment(sketch, "E83", {"start": v(0, 74.25) * mm, "end": v(-36, 74.25) * mm});
            skLineSegment(sketch, "E84", {"start": v(0, 74.25) * mm, "end": v(30, 74.25) * mm});
            skLineSegment(sketch, "E85", {"start": v(12, 92.25) * mm, "end": v(30, 74.25) * mm});
            skCircle(sketch, "E86", {"center": v(-3, 104.6) * mm, "radius": 6 * mm});
            skLineSegment(sketch, "E87.MirrorCS", {"start": v(12, -92.25) * mm, "end": v(30, -74.25) * mm});
            skLineSegment(sketch, "E88.MirrorCS", {"start": v(12, -104.25) * mm, "end": v(12, -92.25) * mm});
            skLineSegment(sketch, "E89.MirrorCS", {"start": v(-18, -104.25) * mm, "end": v(-18, -92.25) * mm});
            skLineSegment(sketch, "E90.MirrorCS", {"start": v(0, -74.25) * mm, "end": v(30, -74.25) * mm});
            skLineSegment(sketch, "E91.MirrorCS", {"start": v(0, -74.25) * mm, "end": v(-36, -74.25) * mm});
            skCircle(sketch, "E92.MirrorC", {"center": v(-3, -104.6) * mm, "radius": 6 * mm});
            skLineSegment(sketch, "E93.MirrorCS", {"start": v(-36, -74.25) * mm, "end": v(-18, -92.25) * mm});
            skArc(sketch, "E94.MirrorCS", {"start": v(12, -104.25) * mm, "mid": v(-3, -119.6) * mm, "end": v(-18, -104.25) * mm});
            skSolve(sketch);
        }
        {
            var Q0;
            Q0=makeQuery(id+"F16.imprint","IMPRINT",FACE,{"disambiguationData":[TD([[makeQuery(id+"F16.imprint","IMPRINT",EDGE,{"derivedFrom":sQuery(id+"F16.wireOp",EDGE,"E87.MirrorCS")}),1.0]])]});
            var Q1;
            {var subQ7=sQuery(id+"F16.wireOp",EDGE,"E83");Q1=makeQuery(id+"F16.imprint","IMPRINT",FACE,{"disambiguationData":[TD([[makeQuery(id+"F16.imprint","IMPRINT",EDGE,{"derivedFrom":subQ7}),-1.0]])]});}
            var Q2;
            Q2=makeQuery(id+"F16.imprint","IMPRINT",FACE,{"disambiguationData":[TD([[makeQuery(id+"F16.imprint","IMPRINT",EDGE,{"derivedFrom":sQuery(id+"F16.wireOp",EDGE,"E79")}),1.0]])]});
            var Q3;
            Q3=makeQuery(id+"F2.opExtrude","CAP_FACE",FACE,{"disambiguationData":[OSD([sQuery(id+"F0.wireOp",EDGE,"E12"),sQuery(id+"F0.wireOp",EDGE,"E13"),sQuery(id+"F0.wireOp",EDGE,"E14"),sQuery(id+"F0.wireOp",EDGE,"E15"),sQuery(id+"F0.wireOp",EDGE,"E17.filletArc"),sQuery(id+"F0.wireOp",EDGE,"E18.filletArc"),sQuery(id+"F0.wireOp",EDGE,"E19.filletArc"),sQuery(id+"F0.wireOp",EDGE,"E20.filletArc"),sQuery(id+"F0.wireOp",EDGE,"E25.0"),sQuery(id+"F0.wireOp",EDGE,"E25.1"),sQuery(id+"F0.wireOp",EDGE,"E25.2"),sQuery(id+"F0.wireOp",EDGE,"E25.3"),sQuery(id+"F0.wireOp",EDGE,"E25.4"),sQuery(id+"F0.wireOp",EDGE,"E25.5"),sQuery(id+"F0.wireOp",EDGE,"E25.6"),sQuery(id+"F0.wireOp",EDGE,"E25.7")])],"isStart":false});
            extrude(context, id + "F17", {"entities" : qUnion([Q0, Q1, Q2]), "endBound" : BoundingType.UP_TO_SURFACE, "endBoundEntityFace" : qUnion([Q3]), "depth" : 25 * mm});
        }
    });
